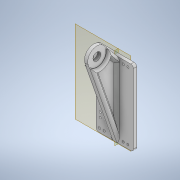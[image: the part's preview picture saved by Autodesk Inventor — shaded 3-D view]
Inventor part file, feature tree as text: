
AUTODESK INVENTOR PART (.ipt)
format: ipt  version: 2022 (Build 260153000, 153)  size: 482,816 bytes
history: native  units: mm
features: other x6, extrude x3, sketch x2, fillet x1, chamfer x1, reference x1
ambient origin geometry x8: Origin, YZ Plane, XZ Plane, XY Plane, X Axis, Y Axis, Z Axis, Center Point
bodies: Body1 (feature_tree)
feature tree (14):
  other  "Твердое тело1"
  other  "РабПлоскость1"
  extrude  "Выдавливание1"  Depth=2.5mm TaperAngle=0.0deg
  other  "РабПлоскость3"
  sketch  "Эскиз6"
  extrude  "Выдавливание3"  Depth=6.0mm
  extrude  "Выдавливание4"  Depth=12.0mm
  fillet  "Сопряжение2"  Radius=7.0mm
  chamfer  "Фаска1"  Distance=40.0mm
  sketch  "Эскиз1"
  reference  "Ссылка1"
  other  "<userpath>\Documents\Inventor\AIM\Aim.iam"
  other  "Aim.iam"
  other  "Base:2"
